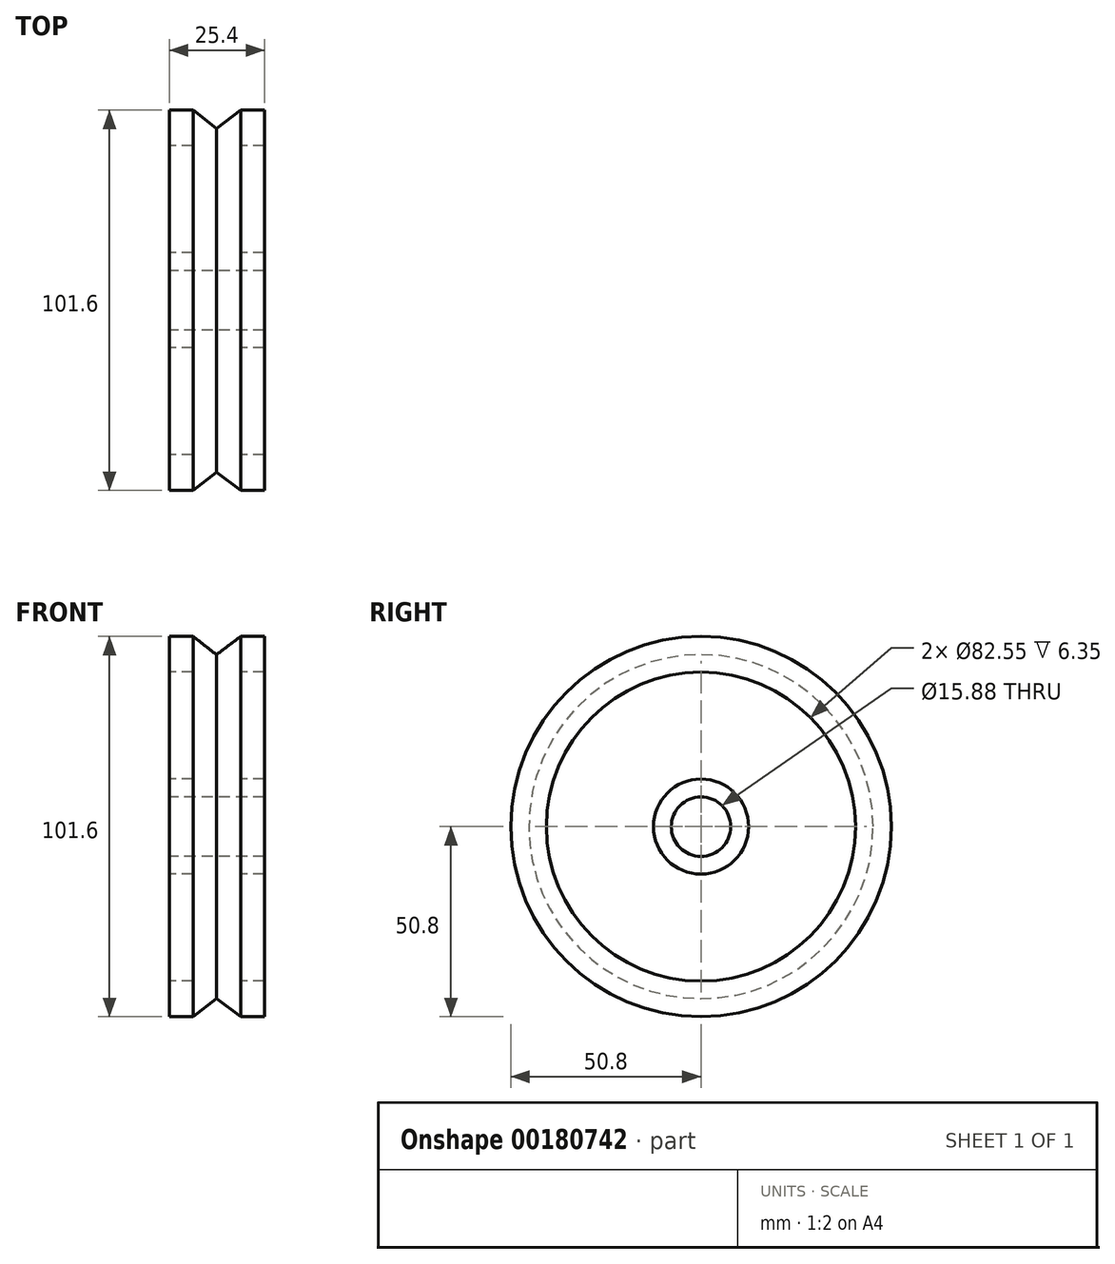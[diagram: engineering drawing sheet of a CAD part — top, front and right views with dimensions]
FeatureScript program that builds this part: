
annotation { "Feature Type Name" : "Feature", "Feature Type Description" : "" }
export const myFeature = defineFeature(function(context is Context, id is Id, definition is map)
    precondition{}
    {
        {
            var Q0;
            Q0=qCreatedBy(makeId("Top.planeOp"),FACE);
            var sketch = newSketch(context, id + "F0", { "sketchPlane" : qUnion([Q0])});
            skLineSegment(sketch, "E0", {"start": v(-45.2, 0) * mm, "end": v(41, 0) * mm, "construction": true});
            skSolve(sketch);
        }
        {
            var Q0;
            Q0=qCreatedBy(makeId("Top.planeOp"),FACE);
            var sketch = newSketch(context, id + "F1", { "sketchPlane" : qUnion([Q0])});
            skLineSegment(sketch, "E1", {"start": v(-12.57, -7.94) * mm, "end": v(12.83, -7.94) * mm});
            skLineSegment(sketch, "E2", {"start": v(12.83, -7.94) * mm, "end": v(12.83, -12.7) * mm});
            skLineSegment(sketch, "E3", {"start": v(12.83, -12.7) * mm, "end": v(6.48, -12.7) * mm});
            skLineSegment(sketch, "E4", {"start": v(6.48, -12.7) * mm, "end": v(6.48, -41.27) * mm});
            skLineSegment(sketch, "E5", {"start": v(-6.22, -41.28) * mm, "end": v(-6.22, -12.7) * mm});
            skLineSegment(sketch, "E6", {"start": v(-6.22, -12.7) * mm, "end": v(-12.57, -12.7) * mm});
            skLineSegment(sketch, "E7", {"start": v(-12.57, -12.7) * mm, "end": v(-12.57, -7.94) * mm});
            skLineSegment(sketch, "E8", {"start": v(12.83, -41.27) * mm, "end": v(6.48, -41.27) * mm});
            skLineSegment(sketch, "E9", {"start": v(-6.22, -41.28) * mm, "end": v(-12.57, -41.28) * mm});
            skLineSegment(sketch, "E10", {"start": v(-12.57, -41.28) * mm, "end": v(-12.57, -50.8) * mm});
            skLineSegment(sketch, "E11", {"start": v(-12.57, -50.8) * mm, "end": v(-6.22, -50.8) * mm});
            skLineSegment(sketch, "E12", {"start": v(6.48, -50.8) * mm, "end": v(12.83, -50.8) * mm});
            skLineSegment(sketch, "E13", {"start": v(12.83, -50.8) * mm, "end": v(12.83, -41.27) * mm});
            skLineSegment(sketch, "E14", {"start": v(-6.22, -50.8) * mm, "end": v(0, -45.95) * mm});
            skLineSegment(sketch, "E15", {"start": v(0, -45.95) * mm, "end": v(6.48, -50.8) * mm});
            skSolve(sketch);
        }
        {
            var Q0;
            Q0 = qSketchRegion(id + "F1", true);
            var Q1;
            Q1=sQuery(id+"F0.wireOp",EDGE,"E0");
            revolve(context, id + "F2", {"entities" : qUnion([Q0]), "axis" : qUnion([Q1]), "revolveType" : RevolveType.FULL});
        }
    });
